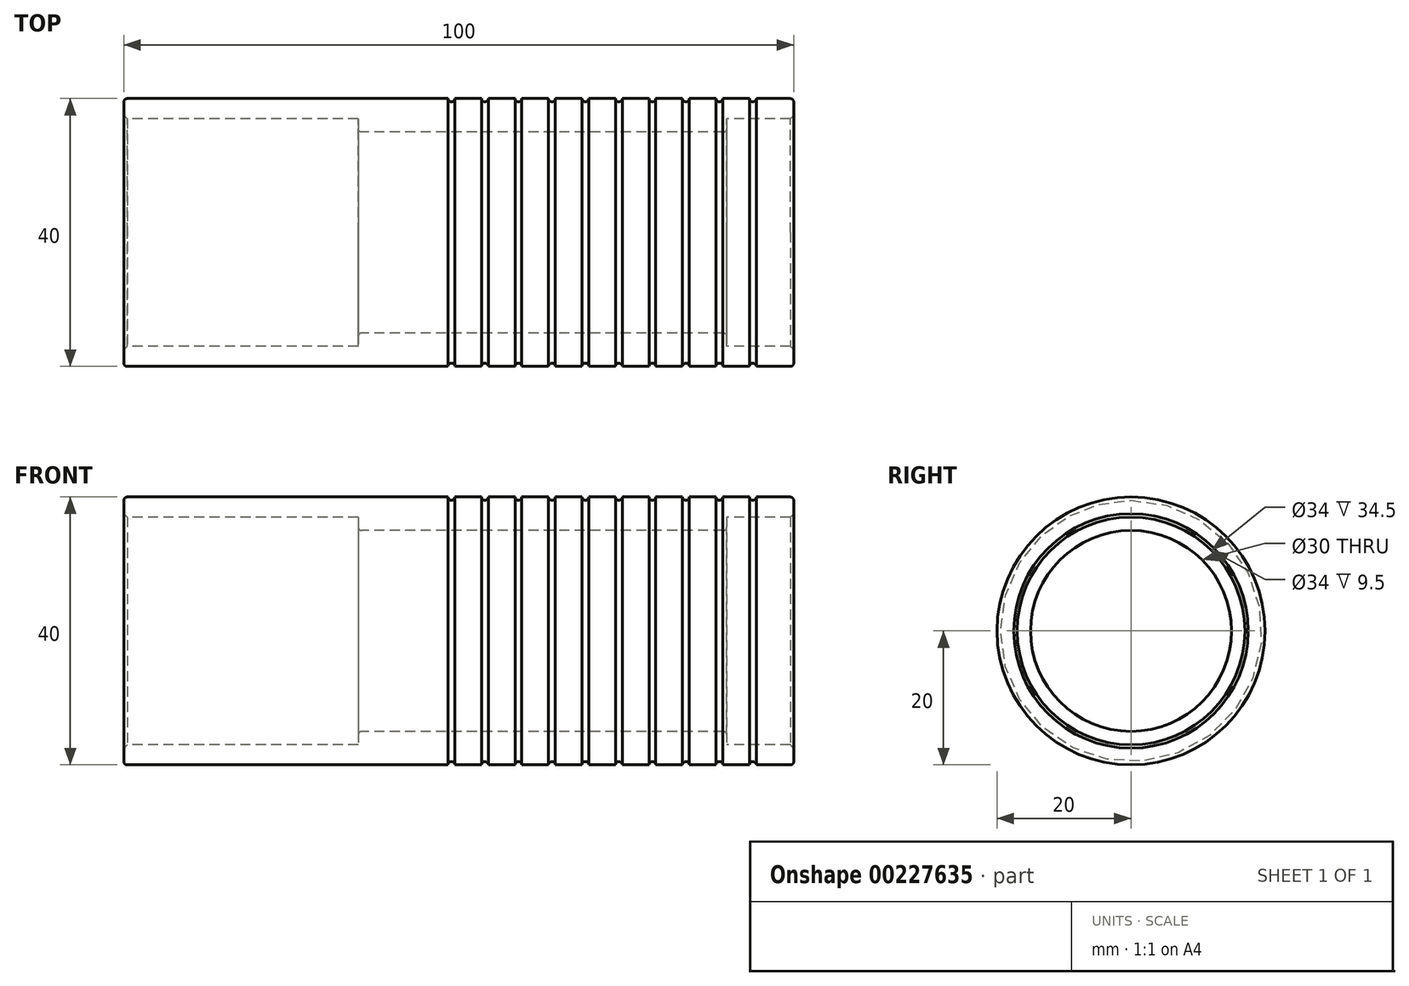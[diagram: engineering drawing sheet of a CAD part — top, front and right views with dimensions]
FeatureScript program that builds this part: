
annotation { "Feature Type Name" : "Feature", "Feature Type Description" : "" }
export const myFeature = defineFeature(function(context is Context, id is Id, definition is map)
    precondition{}
    {
        {
            var Q0;
            Q0=qCreatedBy(makeId("Front.planeOp"),FACE);
            var sketch = newSketch(context, id + "F0", { "sketchPlane" : qUnion([Q0])});
            skLineSegment(sketch, "E0", {"start": v(-48.9, 20) * mm, "end": v(51.1, 20) * mm});
            skLineSegment(sketch, "E1", {"start": v(51.1, 20) * mm, "end": v(51.1, 17) * mm});
            skLineSegment(sketch, "E2", {"start": v(51.1, 17) * mm, "end": v(41.1, 17) * mm});
            skLineSegment(sketch, "E3", {"start": v(41.1, 17) * mm, "end": v(41.1, 15) * mm});
            skLineSegment(sketch, "E4", {"start": v(41.1, 15) * mm, "end": v(-13.9, 15) * mm});
            skLineSegment(sketch, "E5", {"start": v(-13.9, 15) * mm, "end": v(-13.9, 17) * mm});
            skLineSegment(sketch, "E6", {"start": v(-13.9, 17) * mm, "end": v(-48.9, 17) * mm});
            skLineSegment(sketch, "E7", {"start": v(-48.9, 17) * mm, "end": v(-48.9, 20) * mm});
            skLineSegment(sketch, "E8", {"start": v(-60.08, 0) * mm, "end": v(90.4, 0) * mm, "construction": true});
            skSolve(sketch);
        }
        {
            var Q0;
            Q0=makeQuery(id+"F0.imprint","IMPRINT",FACE,{"disambiguationData":[TD([[makeQuery(id+"F0.imprint","IMPRINT",EDGE,{"derivedFrom":sQuery(id+"F0.wireOp",EDGE,"E0")}),-1.0]])]});
            var Q1;
            Q1=sQuery(id+"F0.wireOp",EDGE,"E8");
            revolve(context, id + "F1", {"entities" : qUnion([Q0]), "axis" : qUnion([Q1]), "revolveType" : RevolveType.FULL});
        }
        {
            var Q0;
            Q0=makeQuery(id+"F1.opRevolve","SWEPT_FACE",FACE,{"disambiguationData":[OSD([sQuery(id+"F0.wireOp",EDGE,"E0")])]});
            var Q1;
            Q1=makeQuery(id+"F1.opRevolve","SWEPT_FACE",FACE,{"disambiguationData":[OSD([sQuery(id+"F0.wireOp",EDGE,"E4")])]});
            fillet(context, id + "F2", {"entities" : qUnion([Q0, Q1]), "radius" : .5 * mm, "tangentPropagation" : true, "allowEdgeOverflow" : false});
        }
        {
            var Q0;
            Q0=makeQuery(id+"F1.opRevolve","SWEPT_EDGE",EDGE,{"disambiguationData":[OSD([sQuery(id+"F0.wireOp",EDGE,"E1"),sQuery(id+"F0.wireOp",EDGE,"E2")])]});
            var Q1;
            Q1=makeQuery(id+"F1.opRevolve","SWEPT_EDGE",EDGE,{"disambiguationData":[OSD([sQuery(id+"F0.wireOp",EDGE,"E6"),sQuery(id+"F0.wireOp",EDGE,"E7")])]});
            chamfer(context, id + "F3", {"entities" : qUnion([Q0, Q1]), "width" : .5 * mm, "tangentPropagation" : true});
        }
        {
            var Q0;
            Q0=qCreatedBy(makeId("Front.planeOp"),FACE);
            var sketch = newSketch(context, id + "F4", { "sketchPlane" : qUnion([Q0])});
            skLineSegment(sketch, "E9", {"start": v(-6.49, 0) * mm, "end": v(7.92, 0) * mm, "construction": true});
            skCircle(sketch, "E10", {"center": v(45, 20) * mm, "radius": 0.5 * mm});
            skCircle(sketch, "E11.1.0.0", {"center": v(40, 20) * mm, "radius": 0.5 * mm});
            skCircle(sketch, "E11.2.0.0", {"center": v(35, 20) * mm, "radius": 0.5 * mm});
            skCircle(sketch, "E11.3.0.0", {"center": v(30, 20) * mm, "radius": 0.5 * mm});
            skCircle(sketch, "E11.4.0.0", {"center": v(25, 20) * mm, "radius": 0.5 * mm});
            skCircle(sketch, "E11.5.0.0", {"center": v(20, 20) * mm, "radius": 0.5 * mm});
            skCircle(sketch, "E11.6.0.0", {"center": v(15, 20) * mm, "radius": 0.5 * mm});
            skCircle(sketch, "E11.7.0.0", {"center": v(10, 20) * mm, "radius": 0.5 * mm});
            skCircle(sketch, "E11.8.0.0", {"center": v(5, 20) * mm, "radius": 0.5 * mm});
            skCircle(sketch, "E11.9.0.0", {"center": v(0, 20) * mm, "radius": 0.5 * mm});
            skLineSegment(sketch, "E11.direction1", {"start": v(45, 20) * mm, "end": v(40, 20) * mm, "construction": true});
            skSolve(sketch);
        }
        {
            var Q0;
            Q0 = qSketchRegion(id + "F4", true);
            var Q1;
            Q1=sQuery(id+"F4.wireOp",EDGE,"E9");
            revolve(context, id + "F5", {"operationType" : NewBodyOperationType.REMOVE, "entities" : qUnion([Q0]), "axis" : qUnion([Q1]), "revolveType" : RevolveType.FULL, "oppositeDirection" : true});
        }
    });
